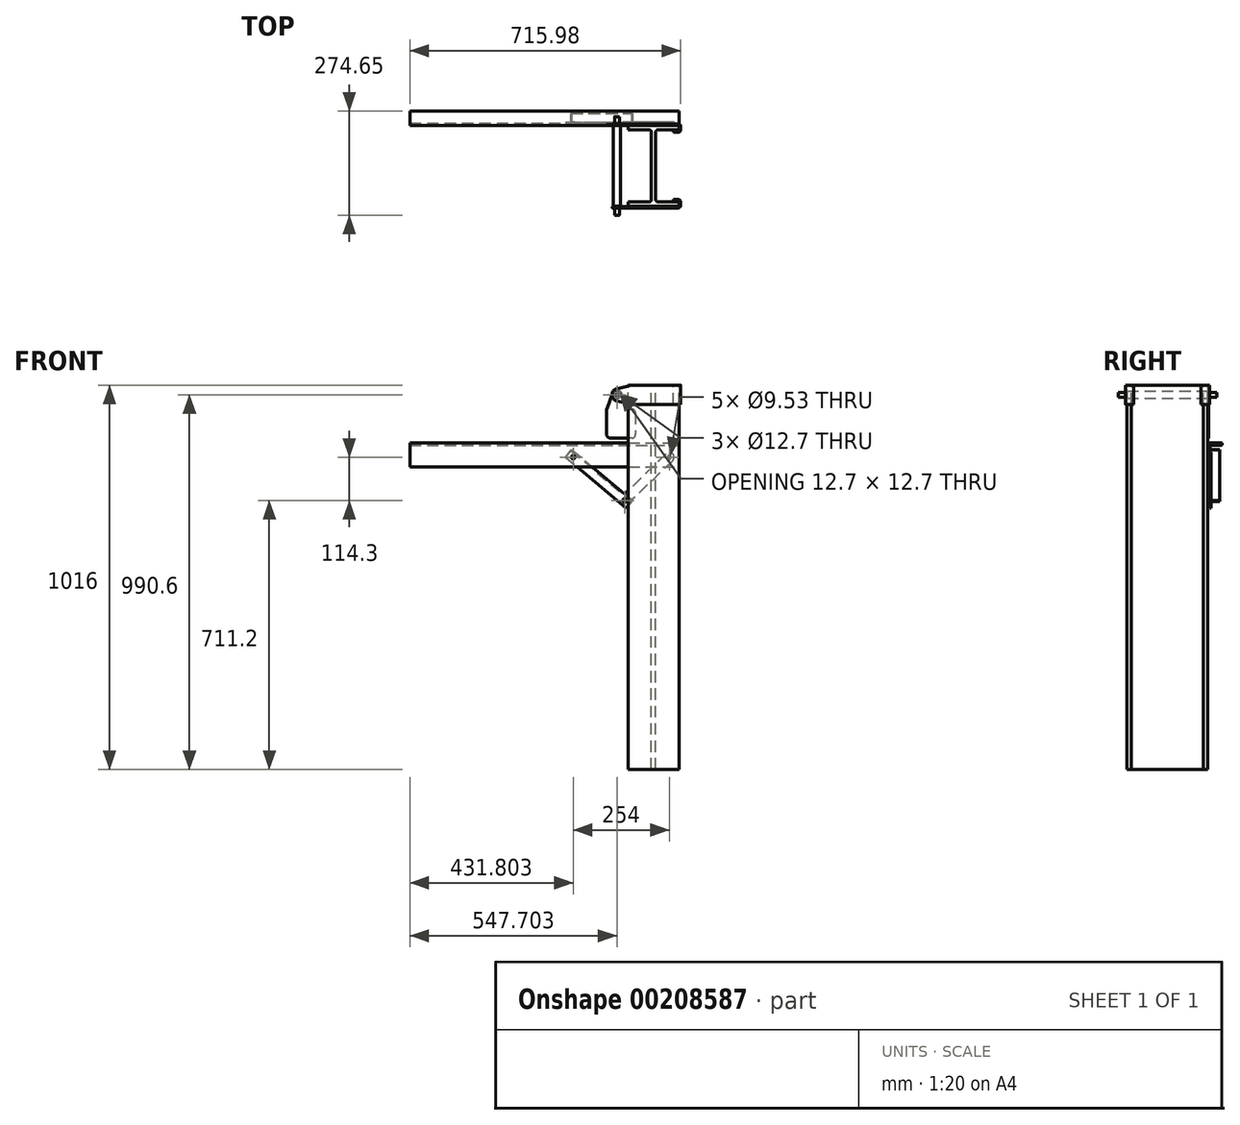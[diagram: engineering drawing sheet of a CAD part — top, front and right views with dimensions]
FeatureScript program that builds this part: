
annotation { "Feature Type Name" : "Feature", "Feature Type Description" : "" }
export const myFeature = defineFeature(function(context is Context, id is Id, definition is map)
    precondition{}
    {
        {
            var Q0;
            Q0=qCreatedBy(makeId("Top.planeOp"),FACE);
            var sketch = newSketch(context, id + "F0", { "sketchPlane" : qUnion([Q0])});
            skLineSegment(sketch, "E0", {"start": v(0, 106.36) * mm, "end": v(0, -106.36) * mm, "construction": true});
            skLineSegment(sketch, "E1", {"start": v(-67, -106.36) * mm, "end": v(67, -106.36) * mm});
            skLineSegment(sketch, "E2", {"start": v(-67, 106.36) * mm, "end": v(67, 106.36) * mm});
            skLineSegment(sketch, "E3.0", {"start": v(-67, 95.25) * mm, "end": v(-5.56, 95.25) * mm});
            skLineSegment(sketch, "E4.0", {"start": v(-67, -95.25) * mm, "end": v(-5.56, -95.25) * mm});
            skLineSegment(sketch, "E5", {"start": v(-67, 106.36) * mm, "end": v(-67, 95.25) * mm});
            skLineSegment(sketch, "E6", {"start": v(67, 106.36) * mm, "end": v(67, 95.25) * mm});
            skLineSegment(sketch, "E7", {"start": v(-67, -95.25) * mm, "end": v(-67, -106.36) * mm});
            skLineSegment(sketch, "E8", {"start": v(67, -95.25) * mm, "end": v(67, -106.36) * mm});
            skLineSegment(sketch, "E9", {"start": v(-5.56, 95.25) * mm, "end": v(-5.56, -95.25) * mm});
            skLineSegment(sketch, "E10", {"start": v(5.56, -95.25) * mm, "end": v(5.56, 95.25) * mm});
            skLineSegment(sketch, "E11", {"start": v(-5.56, 0) * mm, "end": v(5.56, 0) * mm, "construction": true});
            skLineSegment(sketch, "E12.trimOffspring", {"start": v(5.56, 95.25) * mm, "end": v(67, 95.25) * mm});
            skLineSegment(sketch, "E13.trimOffspring", {"start": v(5.56, -95.25) * mm, "end": v(67, -95.25) * mm});
            skSolve(sketch);
        }
        {
            var Q0;
            Q0 = qSketchRegion(id + "F0", true);
            extrude(context, id + "F1", {"entities" : qUnion([Q0]), "oppositeDirection" : true, "depth" : 1016 * mm});
        }
        {
            var Q0;
            Q0=makeQuery(id+"F1.opExtrude","SWEPT_EDGE",EDGE,{"disambiguationData":[OSD([sQuery(id+"F0.wireOp",EDGE,"E10"),sQuery(id+"F0.wireOp",EDGE,"E12.trimOffspring")])]});
            var Q1;
            Q1=makeQuery(id+"F1.opExtrude","SWEPT_EDGE",EDGE,{"disambiguationData":[OSD([sQuery(id+"F0.wireOp",EDGE,"E3.0"),sQuery(id+"F0.wireOp",EDGE,"E9")])]});
            var Q2;
            Q2=makeQuery(id+"F1.opExtrude","SWEPT_EDGE",EDGE,{"disambiguationData":[OSD([sQuery(id+"F0.wireOp",EDGE,"E4.0"),sQuery(id+"F0.wireOp",EDGE,"E9")])]});
            var Q3;
            Q3=makeQuery(id+"F1.opExtrude","SWEPT_EDGE",EDGE,{"disambiguationData":[OSD([sQuery(id+"F0.wireOp",EDGE,"E10"),sQuery(id+"F0.wireOp",EDGE,"E13.trimOffspring")])]});
            fillet(context, id + "F2", {"entities" : qUnion([Q0, Q1, Q2, Q3]), "radius" : 6.35 * mm, "tangentPropagation" : true, "allowEdgeOverflow" : false});
        }
        {
            var Q0;
            Q0=makeQuery(id+"F1.opExtrude","CAP_FACE",FACE,{"disambiguationData":[OSD([sQuery(id+"F0.wireOp",EDGE,"E1"),sQuery(id+"F0.wireOp",EDGE,"E2"),sQuery(id+"F0.wireOp",EDGE,"E3.0"),sQuery(id+"F0.wireOp",EDGE,"E4.0"),sQuery(id+"F0.wireOp",EDGE,"E5"),sQuery(id+"F0.wireOp",EDGE,"E6"),sQuery(id+"F0.wireOp",EDGE,"E7"),sQuery(id+"F0.wireOp",EDGE,"E8"),sQuery(id+"F0.wireOp",EDGE,"E9"),sQuery(id+"F0.wireOp",EDGE,"E10"),sQuery(id+"F0.wireOp",EDGE,"E12.trimOffspring"),sQuery(id+"F0.wireOp",EDGE,"E13.trimOffspring")])],"isStart":true});
            var sketch = newSketch(context, id + "F3", { "sketchPlane" : qUnion([Q0])});
            skLineSegment(sketch, "E14", {"start": v(68.6, 107.96) * mm, "end": v(68.6, 92.09) * mm});
            skLineSegment(sketch, "E15", {"start": v(-109.2, 107.96) * mm, "end": v(68.6, 107.96) * mm});
            skLineSegment(sketch, "E16", {"start": v(68.6, 92.09) * mm, "end": v(52.72, 92.09) * mm});
            skLineSegment(sketch, "E17.0", {"start": v(71.77, 88.91) * mm, "end": v(52.72, 88.91) * mm});
            skLineSegment(sketch, "E17.1", {"start": v(71.77, 111.14) * mm, "end": v(71.77, 88.91) * mm});
            skLineSegment(sketch, "E17.2", {"start": v(-109.2, 111.14) * mm, "end": v(71.77, 111.14) * mm});
            skLineSegment(sketch, "E18", {"start": v(52.72, 88.91) * mm, "end": v(52.72, 92.09) * mm});
            skLineSegment(sketch, "E19", {"start": v(-109.2, 111.14) * mm, "end": v(-109.2, 107.96) * mm});
            skSolve(sketch);
        }
        {
            var Q0;
            Q0 = qSketchRegion(id + "F3", true);
            extrude(context, id + "F4", {"entities" : qUnion([Q0]), "oppositeDirection" : true, "depth" : 50.8 * mm});
        }
        {
            var Q0;
            Q0=makeQuery(id+"F4.opExtrude","SWEPT_EDGE",EDGE,{"disambiguationData":[OSD([sQuery(id+"F3.wireOp",EDGE,"E14"),sQuery(id+"F3.wireOp",EDGE,"E15")])]});
            var Q1;
            Q1=makeQuery(id+"F4.opExtrude","SWEPT_EDGE",EDGE,{"disambiguationData":[OSD([sQuery(id+"F3.wireOp",EDGE,"E14"),sQuery(id+"F3.wireOp",EDGE,"E16")])]});
            fillet(context, id + "F5", {"entities" : qUnion([Q0, Q1]), "radius" : 3.17 * mm, "tangentPropagation" : true, "allowEdgeOverflow" : false});
        }
        {
            var Q0;
            Q0=makeQuery(id+"F4.opExtrude","SWEPT_EDGE",EDGE,{"disambiguationData":[OSD([sQuery(id+"F3.wireOp",EDGE,"E17.1"),sQuery(id+"F3.wireOp",EDGE,"E17.2")])]});
            var Q1;
            Q1=makeQuery(id+"F4.opExtrude","SWEPT_EDGE",EDGE,{"disambiguationData":[OSD([sQuery(id+"F3.wireOp",EDGE,"E17.0"),sQuery(id+"F3.wireOp",EDGE,"E17.1")])]});
            fillet(context, id + "F6", {"entities" : qUnion([Q0, Q1]), "radius" : 6.35 * mm, "tangentPropagation" : true, "allowEdgeOverflow" : false});
        }
        {
            var Q0;
            Q0=makeQuery(id+"F4.opExtrude","CAP_EDGE",EDGE,{"disambiguationData":[OSD([sQuery(id+"F3.wireOp",EDGE,"E19")])],"isStart":true});
            var Q1;
            Q1=makeQuery(id+"F4.opExtrude","CAP_EDGE",EDGE,{"disambiguationData":[OSD([sQuery(id+"F3.wireOp",EDGE,"E19")])],"isStart":false});
            chamfer(context, id + "F7", {"entities" : qUnion([Q0, Q1]), "chamferType" : ChamferType.TWO_OFFSETS, "width1" : 50.8 * mm, "oppositeDirection" : false, "width2" : 12.7 * mm, "tangentPropagation" : true});
        }
        {
            var Q0;
            {var subQ0=sQuery(id+"F3.wireOp",EDGE,"E19");Q0=makeQuery(id+"F7.opChamfer","BLEND_EDGE",EDGE,{"blendedFrom":[makeQuery(id+"F4.opExtrude","CAP_EDGE",EDGE,{"disambiguationData":[OSD([subQ0])],"isStart":true}),makeQuery(id+"F4.opExtrude","CAP_FACE",FACE,{"disambiguationData":[OSD([sQuery(id+"F3.wireOp",EDGE,"E14"),sQuery(id+"F3.wireOp",EDGE,"E15"),sQuery(id+"F3.wireOp",EDGE,"E16"),sQuery(id+"F3.wireOp",EDGE,"E17.0"),sQuery(id+"F3.wireOp",EDGE,"E17.1"),sQuery(id+"F3.wireOp",EDGE,"E17.2"),sQuery(id+"F3.wireOp",EDGE,"E18"),subQ0])],"isStart":true})],"blendedInto":[makeQuery(id+"F4.opExtrude","CAP_FACE",FACE,{"disambiguationData":[OSD([sQuery(id+"F3.wireOp",EDGE,"E14"),sQuery(id+"F3.wireOp",EDGE,"E15"),sQuery(id+"F3.wireOp",EDGE,"E16"),sQuery(id+"F3.wireOp",EDGE,"E17.0"),sQuery(id+"F3.wireOp",EDGE,"E17.1"),sQuery(id+"F3.wireOp",EDGE,"E17.2"),sQuery(id+"F3.wireOp",EDGE,"E18"),subQ0])],"isStart":true})]});}
            var Q1;
            {var subQ0=sQuery(id+"F3.wireOp",EDGE,"E19");Q1=makeQuery(id+"F7.opChamfer","BLEND_EDGE",EDGE,{"blendedFrom":[makeQuery(id+"F4.opExtrude","CAP_EDGE",EDGE,{"disambiguationData":[OSD([subQ0])],"isStart":true}),makeQuery(id+"F4.opExtrude","SWEPT_FACE",FACE,{"disambiguationData":[OSD([subQ0])]})],"blendedInto":[makeQuery(id+"F4.opExtrude","SWEPT_FACE",FACE,{"disambiguationData":[OSD([subQ0])]})]});}
            var Q2;
            {var subQ0=sQuery(id+"F3.wireOp",EDGE,"E19");Q2=makeQuery(id+"F7.opChamfer","BLEND_EDGE",EDGE,{"blendedFrom":[makeQuery(id+"F4.opExtrude","CAP_EDGE",EDGE,{"disambiguationData":[OSD([subQ0])],"isStart":false}),makeQuery(id+"F4.opExtrude","SWEPT_FACE",FACE,{"disambiguationData":[OSD([subQ0])]})],"blendedInto":[makeQuery(id+"F4.opExtrude","SWEPT_FACE",FACE,{"disambiguationData":[OSD([subQ0])]})]});}
            var Q3;
            {var subQ0=sQuery(id+"F3.wireOp",EDGE,"E19");Q3=makeQuery(id+"F7.opChamfer","BLEND_EDGE",EDGE,{"blendedFrom":[makeQuery(id+"F4.opExtrude","CAP_EDGE",EDGE,{"disambiguationData":[OSD([subQ0])],"isStart":false}),makeQuery(id+"F4.opExtrude","CAP_FACE",FACE,{"disambiguationData":[OSD([sQuery(id+"F3.wireOp",EDGE,"E14"),sQuery(id+"F3.wireOp",EDGE,"E15"),sQuery(id+"F3.wireOp",EDGE,"E16"),sQuery(id+"F3.wireOp",EDGE,"E17.0"),sQuery(id+"F3.wireOp",EDGE,"E17.1"),sQuery(id+"F3.wireOp",EDGE,"E17.2"),sQuery(id+"F3.wireOp",EDGE,"E18"),subQ0])],"isStart":false})],"blendedInto":[makeQuery(id+"F4.opExtrude","CAP_FACE",FACE,{"disambiguationData":[OSD([sQuery(id+"F3.wireOp",EDGE,"E14"),sQuery(id+"F3.wireOp",EDGE,"E15"),sQuery(id+"F3.wireOp",EDGE,"E16"),sQuery(id+"F3.wireOp",EDGE,"E17.0"),sQuery(id+"F3.wireOp",EDGE,"E17.1"),sQuery(id+"F3.wireOp",EDGE,"E17.2"),sQuery(id+"F3.wireOp",EDGE,"E18"),subQ0])],"isStart":false})]});}
            fillet(context, id + "F8", {"entities" : qUnion([Q0, Q1, Q2, Q3]), "radius" : 12.7 * mm, "tangentPropagation" : true, "allowEdgeOverflow" : false});
        }
        {
            var Q0;
            Q0=makeQuery(id+"F4.opExtrude","SWEPT_FACE",FACE,{"disambiguationData":[OSD([sQuery(id+"F3.wireOp",EDGE,"E17.2")])]});
            var sketch = newSketch(context, id + "F9", { "sketchPlane" : qUnion([Q0])});
            skLineSegment(sketch, "E20", {"start": v(109.2, -25.4) * mm, "end": v(-65.42, -25.4) * mm, "construction": true});
            skCircle(sketch, "E21", {"center": v(96.5, -25.4) * mm, "radius": 6.35 * mm});
            skSolve(sketch);
        }
        {
            var Q0;
            Q0=sQuery(id+"F9.wireOp",VERTEX,"E21.center");
            var Q1;
            Q1=makeQuery(id+"F4.opExtrude","SWEPT_BODY",BODY,{"disambiguationData":[OSD([sQuery(id+"F3.wireOp",EDGE,"E14"),sQuery(id+"F3.wireOp",EDGE,"E15"),sQuery(id+"F3.wireOp",EDGE,"E16"),sQuery(id+"F3.wireOp",EDGE,"E17.0"),sQuery(id+"F3.wireOp",EDGE,"E17.1"),sQuery(id+"F3.wireOp",EDGE,"E17.2"),sQuery(id+"F3.wireOp",EDGE,"E18"),sQuery(id+"F3.wireOp",EDGE,"E19")])]});
            hole(context, id + "F10", {"style" : HoleStyle.SIMPLE, "endStyle" : HoleEndStyle.BLIND, "holeDiameter" : 12.7 * mm, "holeDepth" : 12.7 * mm, "locations" : qUnion([Q0]), "scope" : qUnion([Q1])});
        }
        {
            var Q0;
            Q0=makeQuery(id+"F4.opExtrude","SWEPT_FACE",FACE,{"disambiguationData":[OSD([sQuery(id+"F3.wireOp",EDGE,"E17.2")])]});
            cPlane(context, id + "F11", {"entities" : qUnion([Q0]), "cplaneType" : CPlaneType.OFFSET, "offset" : 19.05 * mm, "width" : 152.4 * mm, "height" : 152.4 * mm});
        }
        {
            var Q0;
            Q0=qCreatedBy(id+"F11.planeOp",FACE);
            var sketch = newSketch(context, id + "F12", { "sketchPlane" : qUnion([Q0])});
            skCircle(sketch, "E22", {"center": v(96.5, -25.4) * mm, "radius": 6.35 * mm});
            skSolve(sketch);
        }
        {
            var Q0;
            Q0 = qSketchRegion(id + "F12", true);
            extrude(context, id + "F13", {"entities" : qUnion([Q0]), "oppositeDirection" : true, "depth" : 28.57 * mm});
        }
        {
            var Q0;
            Q0=makeQuery(id+"F4.opExtrude","SWEPT_BODY",BODY,{"disambiguationData":[OSD([sQuery(id+"F3.wireOp",EDGE,"E14"),sQuery(id+"F3.wireOp",EDGE,"E15"),sQuery(id+"F3.wireOp",EDGE,"E16"),sQuery(id+"F3.wireOp",EDGE,"E17.0"),sQuery(id+"F3.wireOp",EDGE,"E17.1"),sQuery(id+"F3.wireOp",EDGE,"E17.2"),sQuery(id+"F3.wireOp",EDGE,"E18"),sQuery(id+"F3.wireOp",EDGE,"E19")])]});
            var Q1;
            Q1=qCreatedBy(makeId("Front.planeOp"),FACE);
            mirror(context, id + "F14", {"entities" : qUnion([Q0]), "mirrorPlane" : qUnion([Q1])});
        }
        {
            var Q0;
            Q0=makeQuery(id+"F4.opExtrude","SWEPT_FACE",FACE,{"disambiguationData":[OSD([sQuery(id+"F3.wireOp",EDGE,"E17.2")])]});
            var sketch = newSketch(context, id + "F15", { "sketchPlane" : qUnion([Q0])});
            skPoint(sketch, "E23", {"position": v(96.5, -25.4) * mm});
            skSolve(sketch);
        }
        {
            var Q0;
            Q0=makeQuery(id+"F13.opExtrude","SWEPT_BODY",BODY,{"disambiguationData":[OSD([sQuery(id+"F12.wireOp",EDGE,"E22")])]});
            deleteBodies(context, id + "F16", {"entities" : qUnion([Q0])});
        }
        {
            var Q0;
            Q0=makeQuery(id+"F4.opExtrude","SWEPT_FACE",FACE,{"disambiguationData":[OSD([sQuery(id+"F3.wireOp",EDGE,"E19")])]});
            var Q1;
            Q1=sQuery(id+"F15.wireOp",VERTEX,"E23");
            cPlane(context, id + "F17", {"entities" : qUnion([Q0, Q1]), "cplaneType" : CPlaneType.PLANE_POINT, "offset" : 12.7 * mm, "oppositeDirection" : true, "width" : 152.4 * mm, "height" : 152.4 * mm});
        }
        {
            var Q0;
            Q0=qCreatedBy(id+"F17.planeOp",FACE);
            var sketch = newSketch(context, id + "F18", { "sketchPlane" : qUnion([Q0])});
            skLineSegment(sketch, "E24", {"start": v(-130.19, -25.4) * mm, "end": v(130.19, -25.4) * mm});
            skLineSegment(sketch, "E25", {"start": v(-130.19, -25.4) * mm, "end": v(-130.19, -19.05) * mm});
            skLineSegment(sketch, "E26", {"start": v(-130.19, -19.05) * mm, "end": v(-106.36, -19.05) * mm});
            skLineSegment(sketch, "E27", {"start": v(-106.36, -19.05) * mm, "end": v(-106.36, -15.87) * mm});
            skLineSegment(sketch, "E28", {"start": v(-106.36, -15.88) * mm, "end": v(106.36, -15.88) * mm});
            skLineSegment(sketch, "E29", {"start": v(106.36, -15.87) * mm, "end": v(106.36, -19.05) * mm});
            skLineSegment(sketch, "E30", {"start": v(106.36, -19.05) * mm, "end": v(130.19, -19.05) * mm});
            skLineSegment(sketch, "E31", {"start": v(130.19, -19.05) * mm, "end": v(130.19, -25.4) * mm});
            skSolve(sketch);
        }
        {
            var Q0;
            Q0 = qSketchRegion(id + "F18", true);
            var Q1;
            Q1=sQuery(id+"F18.wireOp",EDGE,"E24");
            revolve(context, id + "F19", {"entities" : qUnion([Q0]), "axis" : qUnion([Q1]), "revolveType" : RevolveType.FULL});
        }
        {
            var Q0;
            Q0=makeQuery(id+"F19.opRevolve","SWEPT_FACE",FACE,{"disambiguationData":[OSD([sQuery(id+"F18.wireOp",EDGE,"E27")])]});
            var sketch = newSketch(context, id + "F20", { "sketchPlane" : qUnion([Q0])});
            skCircle(sketch, "E32.0", {"center": v(96.5, -25.4) * mm, "radius": 6.35 * mm});
            skArc(sketch, "E33", {"start": v(108.44, -21.06) * mm, "mid": v(96.5, -12.7) * mm, "end": v(84.57, -21.06) * mm});
            skLineSegment(sketch, "E34", {"start": v(84.57, -21.06) * mm, "end": v(69.12, -63.5) * mm});
            skLineSegment(sketch, "E35", {"start": v(123.89, -63.5) * mm, "end": v(108.44, -21.06) * mm});
            skLineSegment(sketch, "E36", {"start": v(96.5, -25.4) * mm, "end": v(96.5, -63.5) * mm, "construction": true});
            skLineSegment(sketch, "E37", {"start": v(69.12, -63.5) * mm, "end": v(47.69, -63.5) * mm});
            skLineSegment(sketch, "E38", {"start": v(47.69, -63.5) * mm, "end": v(47.69, -139.7) * mm});
            skLineSegment(sketch, "E39", {"start": v(47.69, -139.7) * mm, "end": v(123.89, -139.7) * mm});
            skLineSegment(sketch, "E40", {"start": v(123.89, -139.7) * mm, "end": v(123.89, -63.5) * mm});
            skLineSegment(sketch, "E41", {"start": v(47.69, -101.6) * mm, "end": v(123.89, -101.6) * mm, "construction": true});
            skPoint(sketch, "E42", {"position": v(79.06, -127) * mm});
            skSolve(sketch);
        }
        {
            var Q0;
            Q0 = qSketchRegion(id + "F20", true);
            extrude(context, id + "F21", {"entities" : qUnion([Q0]), "depth" : 3.17 * mm});
        }
        {
            var Q0;
            Q0=makeQuery(id+"F21.opExtrude","SWEPT_EDGE",EDGE,{"disambiguationData":[OSD([sQuery(id+"F20.wireOp",EDGE,"E34"),sQuery(id+"F20.wireOp",EDGE,"E37")])]});
            var Q1;
            Q1=makeQuery(id+"F21.opExtrude","SWEPT_EDGE",EDGE,{"disambiguationData":[OSD([sQuery(id+"F20.wireOp",EDGE,"E37"),sQuery(id+"F20.wireOp",EDGE,"E38")])]});
            var Q2;
            Q2=makeQuery(id+"F21.opExtrude","SWEPT_EDGE",EDGE,{"disambiguationData":[OSD([sQuery(id+"F20.wireOp",EDGE,"E38"),sQuery(id+"F20.wireOp",EDGE,"E39")])]});
            var Q3;
            Q3=makeQuery(id+"F21.opExtrude","SWEPT_EDGE",EDGE,{"disambiguationData":[OSD([sQuery(id+"F20.wireOp",EDGE,"E39"),sQuery(id+"F20.wireOp",EDGE,"E40")])]});
            var Q4;
            Q4=makeQuery(id+"F21.opExtrude","SWEPT_EDGE",EDGE,{"disambiguationData":[OSD([sQuery(id+"F20.wireOp",EDGE,"E35"),sQuery(id+"F20.wireOp",EDGE,"E40")])]});
            fillet(context, id + "F22", {"entities" : qUnion([Q0, Q1, Q2, Q3, Q4]), "radius" : 9.52 * mm, "tangentPropagation" : true, "allowEdgeOverflow" : false});
        }
        {
            var Q0;
            Q0=makeQuery(id+"F1.opExtrude","SWEPT_FACE",FACE,{"disambiguationData":[OSD([sQuery(id+"F0.wireOp",EDGE,"E6")])]});
            var sketch = newSketch(context, id + "F23", { "sketchPlane" : qUnion([Q0])});
            skLineSegment(sketch, "E43", {"start": v(106.36, -215.9) * mm, "end": v(106.36, -152.4) * mm});
            skLineSegment(sketch, "E44", {"start": v(106.36, -152.4) * mm, "end": v(144.46, -152.4) * mm});
            skLineSegment(sketch, "E45", {"start": v(144.46, -152.4) * mm, "end": v(144.46, -155.57) * mm});
            skLineSegment(sketch, "E46", {"start": v(141.29, -158.75) * mm, "end": v(115.89, -158.75) * mm});
            skLineSegment(sketch, "E47", {"start": v(112.71, -161.93) * mm, "end": v(112.71, -212.72) * mm});
            skLineSegment(sketch, "E48", {"start": v(109.54, -215.9) * mm, "end": v(106.36, -215.9) * mm});
            skPoint(sketch, "E49.visualSharp", {"position": v(112.71, -158.75) * mm});
            skArc(sketch, "E49.filletArc", {"start": v(115.89, -158.75) * mm, "mid": v(113.64, -159.68) * mm, "end": v(112.71, -161.93) * mm});
            skPoint(sketch, "E50.visualSharp", {"position": v(144.46, -158.75) * mm});
            skArc(sketch, "E50.filletArc", {"start": v(141.29, -158.75) * mm, "mid": v(143.53, -157.82) * mm, "end": v(144.46, -155.57) * mm});
            skPoint(sketch, "E51.visualSharp", {"position": v(112.71, -215.9) * mm});
            skArc(sketch, "E51.filletArc", {"start": v(109.54, -215.9) * mm, "mid": v(111.78, -214.97) * mm, "end": v(112.71, -212.72) * mm});
            skSolve(sketch);
        }
        {
            var Q0;
            Q0 = qSketchRegion(id + "F23", true);
            extrude(context, id + "F24", {"entities" : qUnion([Q0]), "oppositeDirection" : true, "depth" : 711.2 * mm});
        }
        {
            var Q0;
            Q0=makeQuery(id+"F1.opExtrude","SWEPT_FACE",FACE,{"disambiguationData":[OSD([sQuery(id+"F0.wireOp",EDGE,"E2")])]});
            var sketch = newSketch(context, id + "F25", { "sketchPlane" : qUnion([Q0])});
            skCircle(sketch, "E52", {"center": v(76.52, -304.8) * mm, "radius": 9.53 * mm});
            skSolve(sketch);
        }
        {
            var Q0;
            Q0=makeQuery(id+"F24.opExtrude","SWEPT_FACE",FACE,{"disambiguationData":[OSD([sQuery(id+"F23.wireOp",EDGE,"E47")])]});
            var sketch = newSketch(context, id + "F26", { "sketchPlane" : qUnion([Q0])});
            skPoint(sketch, "E53", {"position": v(-41.6, -190.5) * mm});
            skPoint(sketch, "E54", {"position": v(212.4, -190.5) * mm});
            skSolve(sketch);
        }
        {
            var Q0;
            Q0=sQuery(id+"F26.wireOp",VERTEX,"E53");
            var Q1;
            Q1=sQuery(id+"F26.wireOp",VERTEX,"E54");
            var Q2;
            Q2=makeQuery(id+"F24.opExtrude","SWEPT_BODY",BODY,{"disambiguationData":[OSD([sQuery(id+"F23.wireOp",EDGE,"E43"),sQuery(id+"F23.wireOp",EDGE,"E44"),sQuery(id+"F23.wireOp",EDGE,"E45"),sQuery(id+"F23.wireOp",EDGE,"E46"),sQuery(id+"F23.wireOp",EDGE,"E47"),sQuery(id+"F23.wireOp",EDGE,"E48"),sQuery(id+"F23.wireOp",EDGE,"E49.filletArc"),sQuery(id+"F23.wireOp",EDGE,"E50.filletArc"),sQuery(id+"F23.wireOp",EDGE,"E51.filletArc")])]});
            hole(context, id + "F27", {"style" : HoleStyle.SIMPLE, "endStyle" : HoleEndStyle.BLIND, "holeDiameter" : 9.52 * mm, "holeDepth" : 9.52 * mm, "locations" : qUnion([Q0, Q1]), "scope" : qUnion([Q2])});
        }
        {
            var Q0;
            Q0=makeQuery(id+"F24.opExtrude","SWEPT_FACE",FACE,{"disambiguationData":[OSD([sQuery(id+"F23.wireOp",EDGE,"E47")])]});
            var sketch = newSketch(context, id + "F28", { "sketchPlane" : qUnion([Q0])});
            skLineSegment(sketch, "E55", {"start": v(-41.6, -190.5) * mm, "end": v(76.52, -304.8) * mm});
            skArc(sketch, "E56.0.startCap", {"start": v(-50.42, -199.63) * mm, "mid": v(-50.72, -181.67) * mm, "end": v(-32.76, -181.37) * mm});
            skArc(sketch, "E56.0.endCap", {"start": v(85.35, -295.67) * mm, "mid": v(85.64, -313.63) * mm, "end": v(67.69, -313.93) * mm});
            skLineSegment(sketch, "E56.0.left", {"start": v(-32.76, -181.37) * mm, "end": v(85.35, -295.67) * mm});
            skLineSegment(sketch, "E56.0.right", {"start": v(-50.42, -199.63) * mm, "end": v(67.69, -313.93) * mm});
            skCircle(sketch, "E57", {"center": v(76.52, -304.8) * mm, "radius": 4.76 * mm});
            skCircle(sketch, "E58.0", {"center": v(-41.6, -190.5) * mm, "radius": 4.76 * mm});
            skSolve(sketch);
        }
        {
            var Q0;
            Q0 = qSketchRegion(id + "F28", true);
            extrude(context, id + "F29", {"entities" : qUnion([Q0]), "depth" : 3.17 * mm});
        }
        {
            var Q0;
            Q0=makeQuery(id+"F24.opExtrude","SWEPT_FACE",FACE,{"disambiguationData":[OSD([sQuery(id+"F23.wireOp",EDGE,"E47")])]});
            var sketch = newSketch(context, id + "F30", { "sketchPlane" : qUnion([Q0])});
            skLineSegment(sketch, "E59", {"start": v(212.4, -190.5) * mm, "end": v(76.52, -304.8) * mm});
            skLineSegment(sketch, "E60.0.left", {"start": v(232.73, -190) * mm, "end": v(72.54, -324.74) * mm});
            skLineSegment(sketch, "E60.0.right", {"start": v(216.38, -170.56) * mm, "end": v(56.2, -305.3) * mm});
            skLineSegment(sketch, "E61", {"start": v(56.2, -305.3) * mm, "end": v(72.54, -324.74) * mm});
            skLineSegment(sketch, "E62", {"start": v(232.73, -190) * mm, "end": v(216.38, -170.56) * mm});
            skCircle(sketch, "E63.0", {"center": v(212.4, -190.5) * mm, "radius": 4.76 * mm});
            skCircle(sketch, "E64", {"center": v(76.52, -304.8) * mm, "radius": 4.76 * mm});
            skSolve(sketch);
        }
        {
            var Q0;
            Q0 = qSketchRegion(id + "F30", true);
            extrude(context, id + "F31", {"entities" : qUnion([Q0]), "depth" : 3.17 * mm});
        }
        {
            var Q0;
            Q0=makeQuery(id+"F31.opExtrude","SWEPT_FACE",FACE,{"disambiguationData":[OSD([sQuery(id+"F30.wireOp",EDGE,"E61")])]});
            var sketch = newSketch(context, id + "F32", { "sketchPlane" : qUnion([Q0])});
            skLineSegment(sketch, "E65", {"start": v(115.89, -269.81) * mm, "end": v(138.11, -269.81) * mm});
            skLineSegment(sketch, "E66", {"start": v(138.11, -269.81) * mm, "end": v(138.11, -272.99) * mm});
            skLineSegment(sketch, "E67", {"start": v(138.11, -272.99) * mm, "end": v(115.89, -272.99) * mm});
            skLineSegment(sketch, "E68", {"start": v(115.89, -272.99) * mm, "end": v(115.89, -269.81) * mm});
            skSolve(sketch);
        }
        {
            var Q0;
            Q0 = qSketchRegion(id + "F32", true);
            var Q1;
            Q1=makeQuery(id+"F31.opExtrude","SWEPT_FACE",FACE,{"disambiguationData":[OSD([sQuery(id+"F30.wireOp",EDGE,"E62")])]});
            extrude(context, id + "F33", {"entities" : qUnion([Q0]), "operationType" : NewBodyOperationType.ADD, "endBound" : BoundingType.UP_TO_SURFACE, "oppositeDirection" : true, "endBoundEntityFace" : qUnion([Q1]), "depth" : 25.4 * mm});
        }
    });
